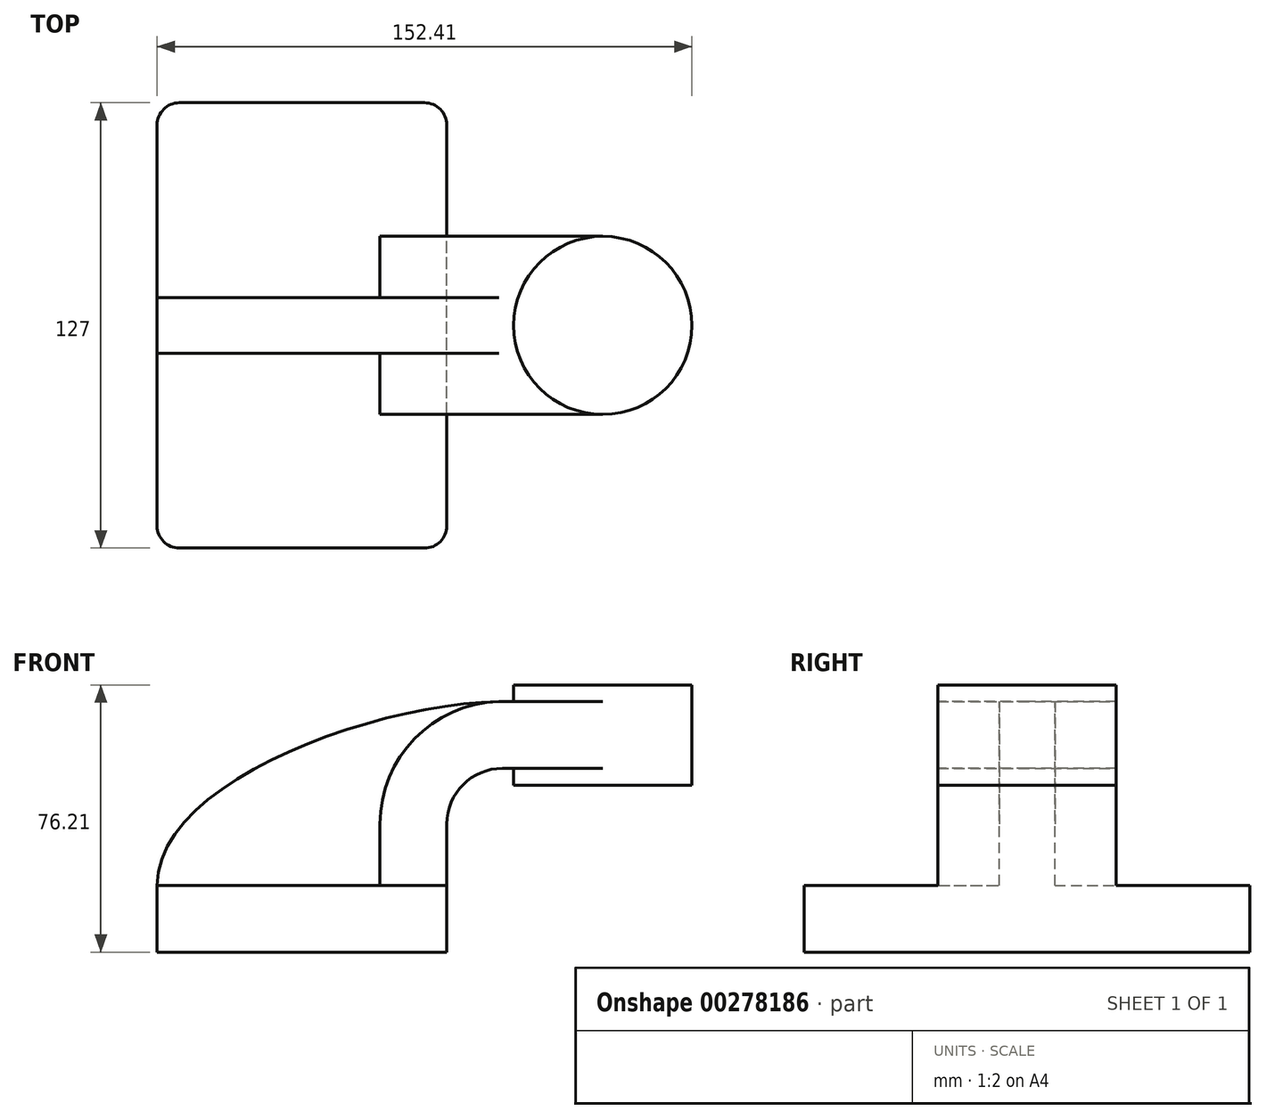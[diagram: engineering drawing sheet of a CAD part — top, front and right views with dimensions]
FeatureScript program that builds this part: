
annotation { "Feature Type Name" : "Feature", "Feature Type Description" : "" }
export const myFeature = defineFeature(function(context is Context, id is Id, definition is map)
    precondition{}
    {
        {
            var Q0;
            Q0=qCreatedBy(makeId("Front.planeOp"),FACE);
            var sketch = newSketch(context, id + "F0", { "sketchPlane" : qUnion([Q0])});
            skLineSegment(sketch, "E0.bottom", {"start": v(41.28, -9.52) * mm, "end": v(-41.28, -9.52) * mm});
            skLineSegment(sketch, "E0.top", {"start": v(41.27, 9.53) * mm, "end": v(-41.28, 9.53) * mm});
            skLineSegment(sketch, "E0.left", {"start": v(41.28, -9.52) * mm, "end": v(41.28, 9.53) * mm});
            skLineSegment(sketch, "E0.right", {"start": v(-41.28, -9.52) * mm, "end": v(-41.28, 9.53) * mm});
            skPoint(sketch, "E0.middle", {"position": v(0, 0) * mm});
            skLineSegment(sketch, "E1.bottom", {"start": v(111.12, 38.1) * mm, "end": v(60.32, 38.1) * mm});
            skLineSegment(sketch, "E1.top", {"start": v(111.12, 66.68) * mm, "end": v(60.32, 66.68) * mm});
            skLineSegment(sketch, "E1.left", {"start": v(111.12, 38.1) * mm, "end": v(111.12, 66.68) * mm});
            skLineSegment(sketch, "E1.right", {"start": v(60.32, 38.1) * mm, "end": v(60.32, 66.68) * mm});
            skPoint(sketch, "E1.middle", {"position": v(85.72, 52.39) * mm});
            skLineSegment(sketch, "E2", {"start": v(41.27, 9.53) * mm, "end": v(41.27, 27) * mm});
            skArc(sketch, "E3", {"start": v(41.27, 27) * mm, "mid": v(45.92, 38.23) * mm, "end": v(57.15, 42.88) * mm});
            skLineSegment(sketch, "E4", {"start": v(57.15, 42.88) * mm, "end": v(85.72, 42.88) * mm});
            skLineSegment(sketch, "E5.0", {"start": v(57.15, 61.93) * mm, "end": v(85.72, 61.93) * mm});
            skArc(sketch, "E5.1", {"start": v(22.22, 27) * mm, "mid": v(32.45, 51.7) * mm, "end": v(57.15, 61.93) * mm});
            skLineSegment(sketch, "E5.2", {"start": v(22.22, 9.53) * mm, "end": v(22.22, 27) * mm});
            skLineSegment(sketch, "E6", {"start": v(85.72, 38.1) * mm, "end": v(85.72, 66.68) * mm});
            skFitSpline(sketch, "E7", {"points": [v(-41.28, 9.52) * mm, v(57.15, 61.93) * mm], "startDerivative": vector(-0.17, 88.73) * mm, "endDerivative": vector(109.27, 1.03) * mm});
            skSolve(sketch);
        }
        {
            var Q0;
            Q0=makeQuery(id+"F0.imprint","IMPRINT",FACE,{"disambiguationData":[TD([[makeQuery(id+"F0.imprint","IMPRINT",EDGE,{"derivedFrom":sQuery(id+"F0.wireOp",EDGE,"E0.bottom")}),-1.0]])]});
            extrude(context, id + "F1", {"entities" : qUnion([Q0]), "endBound" : BoundingType.SYMMETRIC, "depth" : 127 * mm});
        }
        {
            var Q0;
            {var subQ1=sQuery(id+"F0.wireOp",EDGE,"E2");Q0=makeQuery(id+"F0.imprint","IMPRINT",FACE,{"disambiguationData":[TD([[makeQuery(id+"F0.imprint","IMPRINT",EDGE,{"derivedFrom":subQ1}),1.0]])]});}
            var Q1;
            {var subQ0=sQuery(id+"F0.wireOp",EDGE,"E4");var subQ1=sQuery(id+"F0.wireOp",EDGE,"E1.right");var subQ2=makeQuery(id+"F0.imprint","INTERSECT",VERTEX,{"derivedFrom":[subQ1,subQ0]});Q1=makeQuery(id+"F0.imprint","IMPRINT",FACE,{"disambiguationData":[TD([[makeQuery(id+"F0.imprint","IMPRINT",EDGE,{"disambiguationData":[TD([[subQ2,-1.0]])],"derivedFrom":subQ1}),-1.0]])]});}
            extrude(context, id + "F2", {"entities" : qUnion([Q0, Q1]), "operationType" : NewBodyOperationType.ADD, "endBound" : BoundingType.SYMMETRIC, "depth" : 50.8 * mm});
        }
        {
            var Q0;
            {var subQ3=sQuery(id+"F0.wireOp",EDGE,"E5.2");Q0=makeQuery(id+"F0.imprint","IMPRINT",FACE,{"disambiguationData":[TD([[makeQuery(id+"F0.imprint","IMPRINT",EDGE,{"derivedFrom":subQ3}),1.0]])]});}
            extrude(context, id + "F3", {"entities" : qUnion([Q0]), "operationType" : NewBodyOperationType.ADD, "endBound" : BoundingType.SYMMETRIC, "depth" : 15.88 * mm});
        }
        {
            var Q0;
            {var subQ0=sQuery(id+"F0.wireOp",EDGE,"E1.left");Q0=makeQuery(id+"F0.imprint","IMPRINT",FACE,{"disambiguationData":[TD([[makeQuery(id+"F0.imprint","IMPRINT",EDGE,{"derivedFrom":subQ0}),1.0]])]});}
            var Q1;
            Q1=sQuery(id+"F0.wireOp",EDGE,"E6");
            revolve(context, id + "F4", {"operationType" : NewBodyOperationType.ADD, "entities" : qUnion([Q0]), "axis" : qUnion([Q1]), "revolveType" : RevolveType.FULL});
        }
        {
            var Q0;
            Q0=makeQuery(id+"F1.opExtrude","CAP_EDGE",EDGE,{"disambiguationData":[OSD([sQuery(id+"F0.wireOp",EDGE,"E0.left")])],"isStart":false});
            var Q1;
            Q1=makeQuery(id+"F1.opExtrude","CAP_EDGE",EDGE,{"disambiguationData":[OSD([sQuery(id+"F0.wireOp",EDGE,"E0.left")])],"isStart":true});
            var Q2;
            Q2=makeQuery(id+"F1.opExtrude","CAP_EDGE",EDGE,{"disambiguationData":[OSD([sQuery(id+"F0.wireOp",EDGE,"E0.right")])],"isStart":false});
            var Q3;
            Q3=makeQuery(id+"F1.opExtrude","CAP_EDGE",EDGE,{"disambiguationData":[OSD([sQuery(id+"F0.wireOp",EDGE,"E0.right")])],"isStart":true});
            fillet(context, id + "F5", {"entities" : qUnion([Q0, Q1, Q2, Q3]), "radius" : 6.35 * mm, "tangentPropagation" : true, "allowEdgeOverflow" : false});
        }
    });
